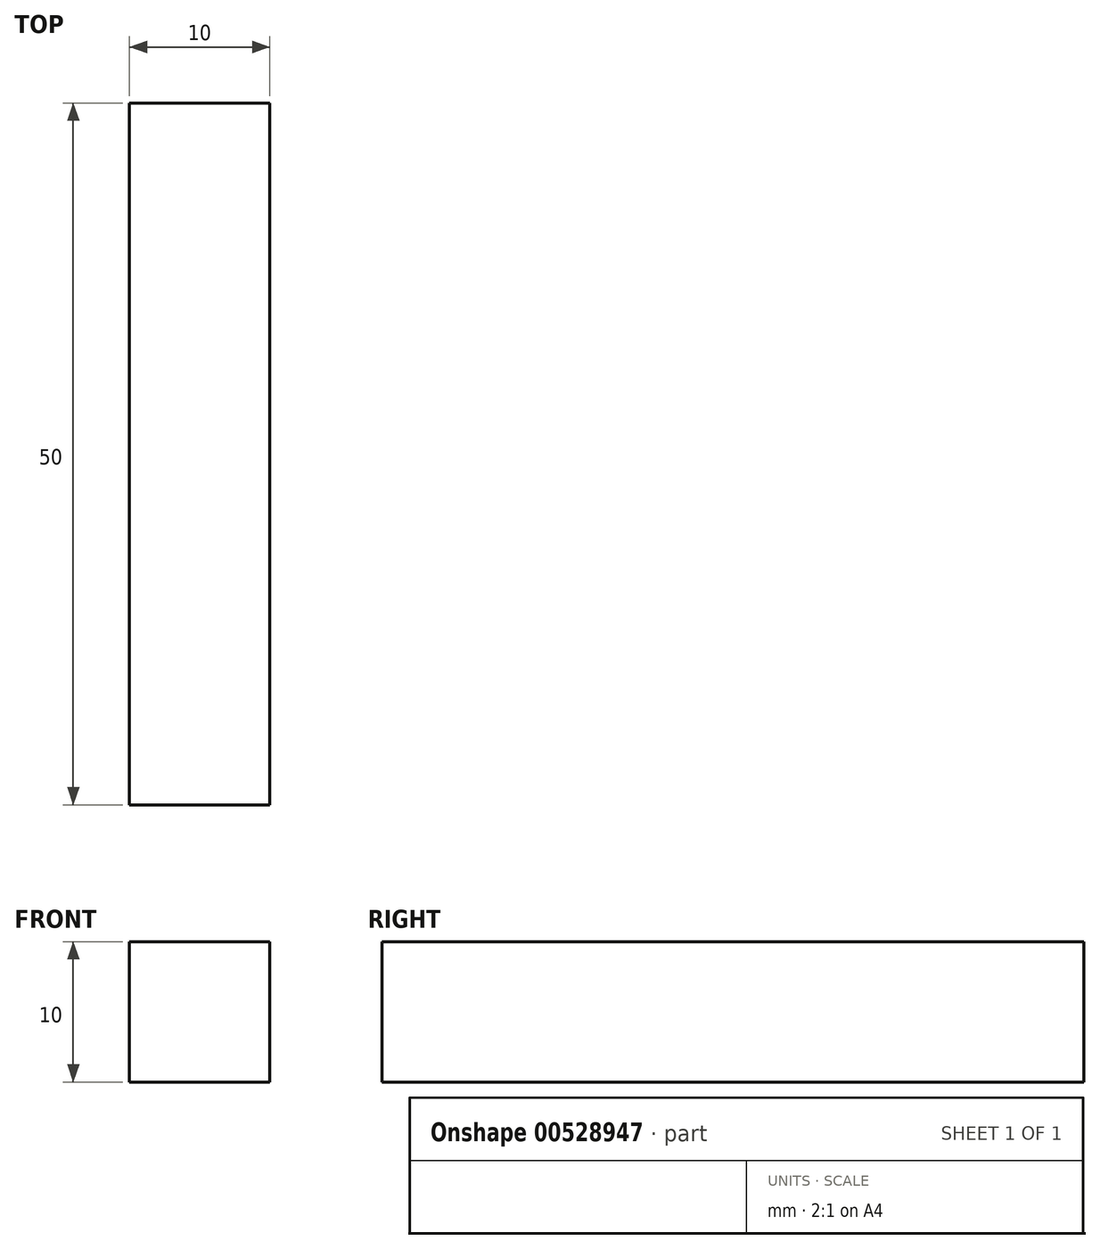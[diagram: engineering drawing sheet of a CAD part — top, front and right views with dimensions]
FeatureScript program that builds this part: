
annotation { "Feature Type Name" : "Feature", "Feature Type Description" : "" }
export const myFeature = defineFeature(function(context is Context, id is Id, definition is map)
    precondition{}
    {
        {
            var Q0;
            Q0=qCreatedBy(makeId("Top.planeOp"),FACE);
            var sketch = newSketch(context, id + "F0", { "sketchPlane" : qUnion([Q0])});
            skLineSegment(sketch, "E0.bottom", {"start": v(-57.03, 14) * mm, "end": v(-67.03, 14) * mm});
            skLineSegment(sketch, "E0.top", {"start": v(-57.03, 64) * mm, "end": v(-67.03, 64) * mm});
            skLineSegment(sketch, "E0.left", {"start": v(-57.03, 14) * mm, "end": v(-57.03, 64) * mm});
            skLineSegment(sketch, "E0.right", {"start": v(-67.03, 14) * mm, "end": v(-67.03, 64) * mm});
            skPoint(sketch, "E0.middle", {"position": v(-62.03, 39) * mm});
            skSolve(sketch);
        }
        {
            var Q0;
            Q0=makeQuery(id+"F0.imprint","IMPRINT",FACE,{"disambiguationData":[TD([[makeQuery(id+"F0.imprint","IMPRINT",EDGE,{"derivedFrom":sQuery(id+"F0.wireOp",EDGE,"E0.bottom")}),-1.0]])]});
            extrude(context, id + "F1", {"entities" : qUnion([Q0]), "depth" : 10 * mm, "offsetDistance" : 25 * mm});
        }
    });
